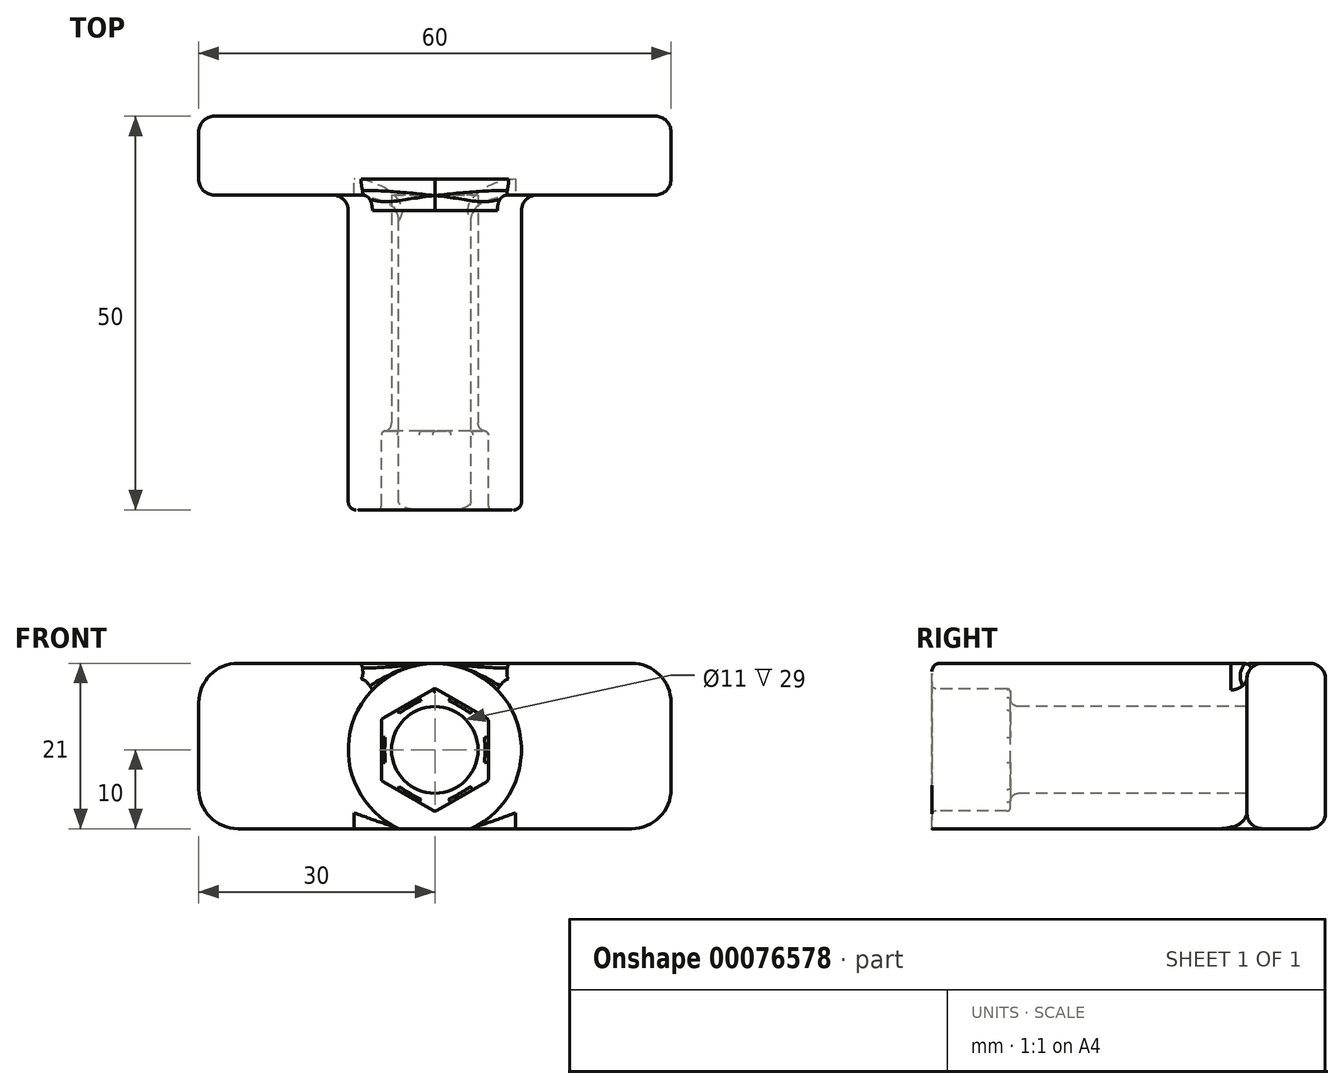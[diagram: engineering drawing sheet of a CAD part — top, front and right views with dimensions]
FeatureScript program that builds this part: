
annotation { "Feature Type Name" : "Feature", "Feature Type Description" : "" }
export const myFeature = defineFeature(function(context is Context, id is Id, definition is map)
    precondition{}
    {
        {
            var Q0;
            Q0=qCreatedBy(makeId("Front.planeOp"),FACE);
            var sketch = newSketch(context, id + "F0", { "sketchPlane" : qUnion([Q0])});
            skCircle(sketch, "E0.cCircle", {"center": v(0, 0) * mm, "radius": 6.8 * mm, "construction": true});
            skLineSegment(sketch, "E0.0", {"start": v(6.8, 3.93) * mm, "end": v(6.8, -3.93) * mm});
            skLineSegment(sketch, "E0.1", {"start": v(6.8, -3.93) * mm, "end": v(0, -7.85) * mm});
            skLineSegment(sketch, "E0.2", {"start": v(0, -7.85) * mm, "end": v(-6.8, -3.93) * mm});
            skLineSegment(sketch, "E0.3", {"start": v(-6.8, -3.93) * mm, "end": v(-6.8, 3.93) * mm});
            skLineSegment(sketch, "E0.4", {"start": v(-6.8, 3.93) * mm, "end": v(0, 7.85) * mm});
            skLineSegment(sketch, "E0.5", {"start": v(0, 7.85) * mm, "end": v(6.8, 3.93) * mm});
            skPoint(sketch, "E0.0.midPoint", {"position": v(6.8, 0) * mm});
            skCircle(sketch, "E1", {"center": v(0, 0) * mm, "radius": 11 * mm});
            skCircle(sketch, "E2", {"center": v(0, 0) * mm, "radius": 5.5 * mm});
            skLineSegment(sketch, "E3", {"start": v(-4.58, -10) * mm, "end": v(4.58, -10) * mm});
            skPoint(sketch, "E4", {"position": v(0, -11) * mm});
            skSolve(sketch);
        }
        {
            var Q0;
            Q0=makeQuery(id+"F0.imprint","IMPRINT",FACE,{"disambiguationData":[TD([[makeQuery(id+"F0.imprint","IMPRINT",EDGE,{"derivedFrom":sQuery(id+"F0.wireOp",EDGE,"E0.0")}),1.0]])]});
            extrude(context, id + "F1", {"entities" : qUnion([Q0]), "depth" : 10 * mm});
        }
        {
            var Q0;
            Q0=makeQuery(id+"F0.imprint","IMPRINT",FACE,{"disambiguationData":[TD([[makeQuery(id+"F0.imprint","IMPRINT",EDGE,{"derivedFrom":sQuery(id+"F0.wireOp",EDGE,"E0.0")}),-1.0]])]});
            var Q1;
            Q1=makeQuery(id+"F0.imprint","IMPRINT",FACE,{"disambiguationData":[TD([[makeQuery(id+"F0.imprint","IMPRINT",EDGE,{"derivedFrom":sQuery(id+"F0.wireOp",EDGE,"E0.0")}),1.0]])]});
            var Q2;
            Q2=sQuery(id+"F0.wireOp",EDGE,"E2");
            extrude(context, id + "F2", {"entities" : qUnion([Q0, Q1]), "operationType" : NewBodyOperationType.ADD, "surfaceEntities" : qUnion([Q2]), "oppositeDirection" : true, "depth" : 30 * mm});
        }
        {
            var Q0;
            Q0=makeQuery(id+"F2.opExtrude","CAP_FACE",FACE,{"disambiguationData":[OSD([sQuery(id+"F0.wireOp",EDGE,"E1"),sQuery(id+"F0.wireOp",EDGE,"E2"),sQuery(id+"F0.wireOp",EDGE,"E3")])],"isStart":false});
            var sketch = newSketch(context, id + "F3", { "sketchPlane" : qUnion([Q0])});
            skLineSegment(sketch, "E5.bottom", {"start": v(30, -10) * mm, "end": v(-30, -10) * mm});
            skLineSegment(sketch, "E5.top", {"start": v(30, 11) * mm, "end": v(-30, 11) * mm});
            skLineSegment(sketch, "E5.left", {"start": v(30, -10) * mm, "end": v(30, 11) * mm});
            skLineSegment(sketch, "E5.right", {"start": v(-30, -10) * mm, "end": v(-30, 11) * mm});
            skPoint(sketch, "E5.middle", {"position": v(0, 0.5) * mm});
            skLineSegment(sketch, "E6", {"start": v(0, -10) * mm, "end": v(0, 0.5) * mm, "construction": true});
            skPoint(sketch, "E7", {"position": v(0, 11) * mm});
            skSolve(sketch);
        }
        {
            var Q0;
            Q0 = qSketchRegion(id + "F3", true);
            extrude(context, id + "F4", {"entities" : qUnion([Q0]), "operationType" : NewBodyOperationType.ADD, "depth" : 10 * mm});
        }
        {
            var Q0;
            Q0=makeQuery(id+"F4.opExtrude","SWEPT_EDGE",EDGE,{"disambiguationData":[OSD([sQuery(id+"F3.wireOp",EDGE,"E5.top"),sQuery(id+"F3.wireOp",EDGE,"E5.right")])]});
            var Q1;
            Q1=makeQuery(id+"F4.opExtrude","SWEPT_EDGE",EDGE,{"disambiguationData":[OSD([sQuery(id+"F3.wireOp",EDGE,"E5.bottom"),sQuery(id+"F3.wireOp",EDGE,"E5.right")])]});
            var Q2;
            Q2=makeQuery(id+"F4.opExtrude","SWEPT_EDGE",EDGE,{"disambiguationData":[OSD([sQuery(id+"F3.wireOp",EDGE,"E5.top"),sQuery(id+"F3.wireOp",EDGE,"E5.left")])]});
            var Q3;
            Q3=makeQuery(id+"F4.opExtrude","SWEPT_EDGE",EDGE,{"disambiguationData":[OSD([sQuery(id+"F3.wireOp",EDGE,"E5.bottom"),sQuery(id+"F3.wireOp",EDGE,"E5.left")])]});
            fillet(context, id + "F5", {"entities" : qUnion([Q0, Q1, Q2, Q3]), "radius" : 5 * mm, "tangentPropagation" : true, "allowEdgeOverflow" : false});
        }
        {
            var Q0;
            Q0=makeQuery(id+"F4.opExtrude","CAP_FACE",FACE,{"disambiguationData":[OSD([sQuery(id+"F3.wireOp",EDGE,"E5.bottom"),sQuery(id+"F3.wireOp",EDGE,"E5.top"),sQuery(id+"F3.wireOp",EDGE,"E5.left"),sQuery(id+"F3.wireOp",EDGE,"E5.right")])],"isStart":false});
            var Q1;
            {var subQ2=sQuery(id+"F3.wireOp",EDGE,"E5.top");var subQ3=sQuery(id+"F3.wireOp",EDGE,"E5.left");var subQ4=sQuery(id+"F3.wireOp",EDGE,"E5.bottom");var subQ5=makeQuery(id+"F4.opExtrude","CAP_FACE",FACE,{"disambiguationData":[OSD([subQ4,subQ2,subQ3,sQuery(id+"F3.wireOp",EDGE,"E5.right")])],"isStart":true});Q1=makeQuery(id+"F4.boolean.opBoolean","SPLIT",FACE,{"disambiguationData":[TD([makeQuery(id+"F4.opExtrude","SWEPT_FACE",FACE,{"disambiguationData":[OSD([subQ3])]})])],"derivedFrom":subQ5});}
            var Q2;
            {var subQ2=sQuery(id+"F3.wireOp",EDGE,"E5.top");var subQ3=sQuery(id+"F3.wireOp",EDGE,"E5.right");var subQ4=sQuery(id+"F3.wireOp",EDGE,"E5.bottom");var subQ5=makeQuery(id+"F4.opExtrude","CAP_FACE",FACE,{"disambiguationData":[OSD([subQ4,subQ2,sQuery(id+"F3.wireOp",EDGE,"E5.left"),subQ3])],"isStart":true});Q2=makeQuery(id+"F4.boolean.opBoolean","SPLIT",FACE,{"disambiguationData":[TD([makeQuery(id+"F4.opExtrude","SWEPT_FACE",FACE,{"disambiguationData":[OSD([subQ3])]})])],"derivedFrom":subQ5});}
            fillet(context, id + "F6", {"entities" : qUnion([Q0, Q1, Q2]), "radius" : 2 * mm, "tangentPropagation" : true, "allowEdgeOverflow" : false});
        }
        {
            var Q0;
            Q0=makeQuery(id+"F1.opExtrude","CAP_EDGE",EDGE,{"disambiguationData":[OSD([sQuery(id+"F0.wireOp",EDGE,"E1")])],"isStart":false});
            var Q1;
            Q1=makeQuery(id+"F2.opExtrude","CAP_EDGE",EDGE,{"disambiguationData":[OSD([sQuery(id+"F0.wireOp",EDGE,"E2")])],"isStart":true});
            fillet(context, id + "F7", {"entities" : qUnion([Q0, Q1]), "radius" : 1 * mm, "tangentPropagation" : true, "allowEdgeOverflow" : false});
        }
        {
            var Q0;
            Q0=makeQuery(id+"F1.opExtrude","SWEPT_FACE",FACE,{"disambiguationData":[OSD([sQuery(id+"F0.wireOp",EDGE,"E0.5")])]});
            var Q1;
            Q1=makeQuery(id+"F1.opExtrude","SWEPT_FACE",FACE,{"disambiguationData":[OSD([sQuery(id+"F0.wireOp",EDGE,"E0.4")])]});
            var Q2;
            Q2=makeQuery(id+"F1.opExtrude","SWEPT_FACE",FACE,{"disambiguationData":[OSD([sQuery(id+"F0.wireOp",EDGE,"E0.3")])]});
            var Q3;
            Q3=makeQuery(id+"F1.opExtrude","SWEPT_FACE",FACE,{"disambiguationData":[OSD([sQuery(id+"F0.wireOp",EDGE,"E0.2")])]});
            var Q4;
            Q4=makeQuery(id+"F1.opExtrude","SWEPT_FACE",FACE,{"disambiguationData":[OSD([sQuery(id+"F0.wireOp",EDGE,"E0.1")])]});
            var Q5;
            Q5=makeQuery(id+"F1.opExtrude","SWEPT_FACE",FACE,{"disambiguationData":[OSD([sQuery(id+"F0.wireOp",EDGE,"E0.0")])]});
            fillet(context, id + "F8", {"entities" : qUnion([Q0, Q1, Q2, Q3, Q4, Q5]), "radius" : .5 * mm, "tangentPropagation" : true, "allowEdgeOverflow" : false});
        }
    });
